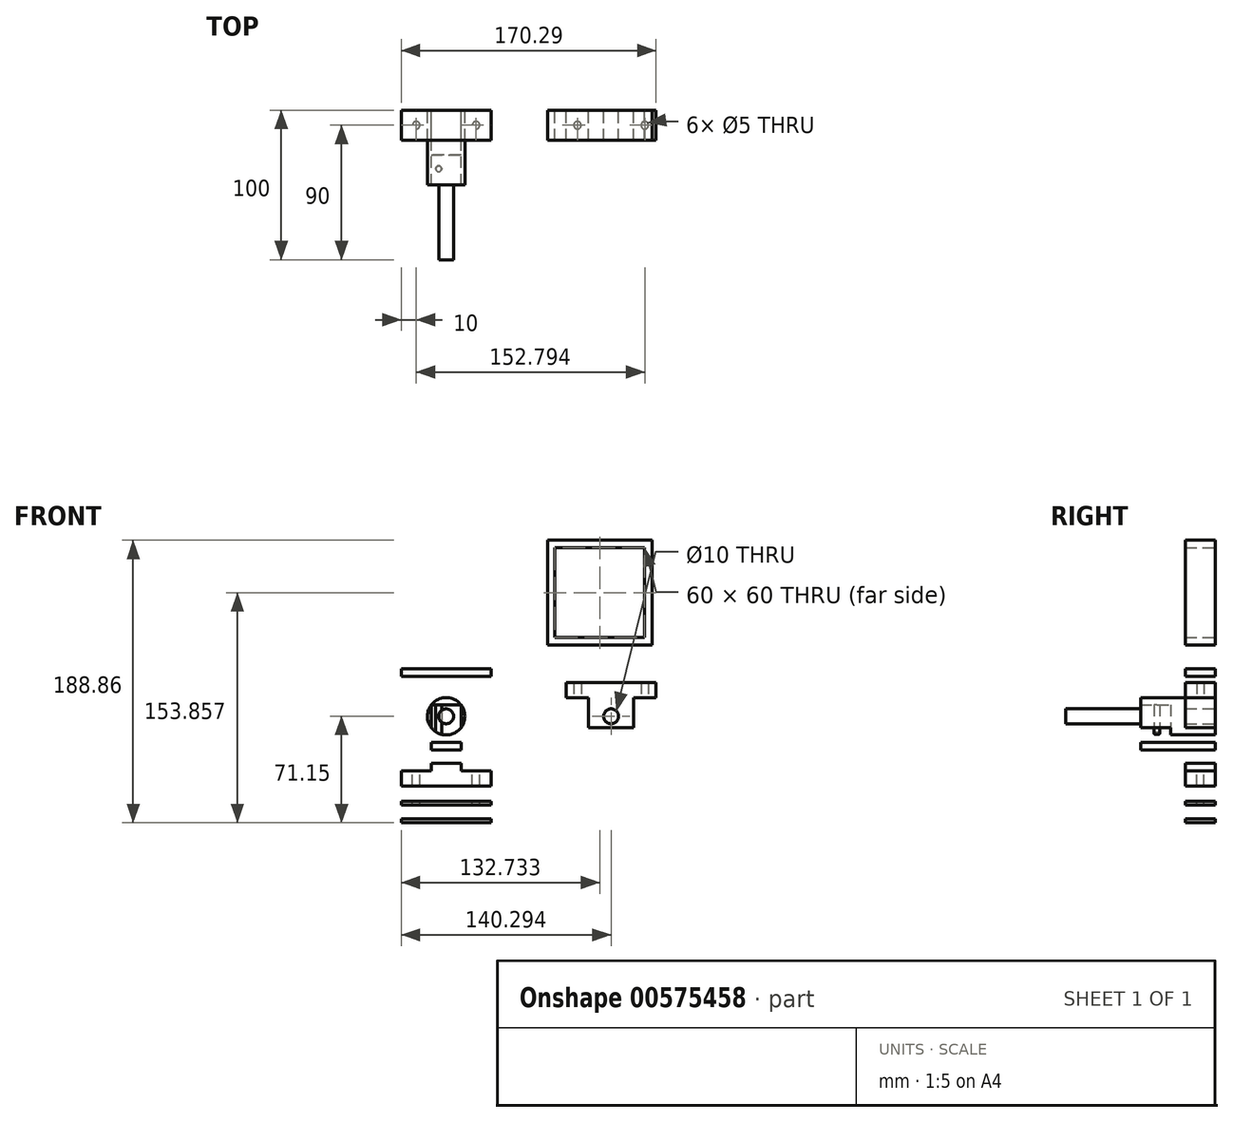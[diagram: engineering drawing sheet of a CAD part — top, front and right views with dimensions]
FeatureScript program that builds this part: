
annotation { "Feature Type Name" : "Feature", "Feature Type Description" : "" }
export const myFeature = defineFeature(function(context is Context, id is Id, definition is map)
    precondition{}
    {
        {
            var Q0;
            Q0=qCreatedBy(makeId("Front.planeOp"),FACE);
            var sketch = newSketch(context, id + "F0", { "sketchPlane" : qUnion([Q0])});
            skCircle(sketch, "E0", {"center": v(0, 0) * mm, "radius": 12.5 * mm});
            skCircle(sketch, "E1", {"center": v(110.3, 0) * mm, "radius": 5 * mm});
            skLineSegment(sketch, "E2.bottom", {"start": v(-30, 31.74) * mm, "end": v(30, 31.74) * mm});
            skLineSegment(sketch, "E2.top", {"start": v(-30, 26.74) * mm, "end": v(30, 26.74) * mm});
            skLineSegment(sketch, "E2.left", {"start": v(-30, 31.74) * mm, "end": v(-30, 26.74) * mm});
            skLineSegment(sketch, "E2.right", {"start": v(30, 31.74) * mm, "end": v(30, 26.74) * mm});
            skPoint(sketch, "E2.middle", {"position": v(0, 29.24) * mm});
            skLineSegment(sketch, "E3", {"start": v(110.3, 10) * mm, "end": v(110.3, -10) * mm, "construction": true});
            skCircle(sketch, "E4", {"center": v(110.3, 0) * mm, "radius": 12.5 * mm, "construction": true});
            skLineSegment(sketch, "E5", {"start": v(97.8, 0) * mm, "end": v(122.8, 0) * mm, "construction": true});
            skLineSegment(sketch, "E6", {"start": v(110.3, 12.5) * mm, "end": v(79.29, 12.5) * mm, "construction": true});
            skLineSegment(sketch, "E7", {"start": v(110.3, 5) * mm, "end": v(79.29, 5) * mm, "construction": true});
            skLineSegment(sketch, "E8", {"start": v(110.3, -5) * mm, "end": v(79.29, -5) * mm, "construction": true});
            skLineSegment(sketch, "E9", {"start": v(110.3, -12.5) * mm, "end": v(79.29, -12.5) * mm, "construction": true});
            skLineSegment(sketch, "E10", {"start": v(110.3, -7.5) * mm, "end": v(125.3, -7.5) * mm});
            skLineSegment(sketch, "E11", {"start": v(110.3, 22.5) * mm, "end": v(140.3, 22.5) * mm});
            skLineSegment(sketch, "E12", {"start": v(125.3, 12.5) * mm, "end": v(140.3, 12.5) * mm});
            skLineSegment(sketch, "E13", {"start": v(125.3, -7.5) * mm, "end": v(125.3, 12.5) * mm});
            skLineSegment(sketch, "E14", {"start": v(140.3, 22.5) * mm, "end": v(140.3, 12.5) * mm});
            skPoint(sketch, "E15.orphan", {"position": v(110.3, 12.5) * mm});
            skLineSegment(sketch, "E16.MirrorCS", {"start": v(95.3, 12.5) * mm, "end": v(80.3, 12.5) * mm});
            skLineSegment(sketch, "E17.MirrorCS", {"start": v(80.3, 22.5) * mm, "end": v(80.3, 12.5) * mm});
            skLineSegment(sketch, "E18.MirrorCS", {"start": v(110.3, 22.5) * mm, "end": v(80.3, 22.5) * mm});
            skLineSegment(sketch, "E19.MirrorCS", {"start": v(95.3, -7.5) * mm, "end": v(95.3, 12.5) * mm});
            skLineSegment(sketch, "E20.MirrorCS", {"start": v(110.3, -7.5) * mm, "end": v(95.3, -7.5) * mm});
            skLineSegment(sketch, "E21.top", {"start": v(0, -31.53) * mm, "end": v(10, -31.53) * mm});
            skLineSegment(sketch, "E21.right", {"start": v(10, -36.53) * mm, "end": v(10, -31.53) * mm});
            skLineSegment(sketch, "E22", {"start": v(10, -36.53) * mm, "end": v(30, -36.53) * mm});
            skLineSegment(sketch, "E23", {"start": v(30, -36.53) * mm, "end": v(30, -46.53) * mm});
            skLineSegment(sketch, "E24", {"start": v(30, -46.53) * mm, "end": v(0, -46.53) * mm});
            skLineSegment(sketch, "E25.MirrorCS", {"start": v(0, -31.53) * mm, "end": v(-10, -31.53) * mm});
            skLineSegment(sketch, "E26.MirrorCS", {"start": v(-10, -36.53) * mm, "end": v(-10, -31.53) * mm});
            skLineSegment(sketch, "E27.MirrorCS", {"start": v(-10, -36.53) * mm, "end": v(-30, -36.53) * mm});
            skLineSegment(sketch, "E28.MirrorCS", {"start": v(-30, -36.53) * mm, "end": v(-30, -46.53) * mm});
            skLineSegment(sketch, "E29.MirrorCS", {"start": v(-30, -46.53) * mm, "end": v(0, -46.53) * mm});
            skLineSegment(sketch, "E30", {"start": v(0, -22.52) * mm, "end": v(10, -22.52) * mm});
            skLineSegment(sketch, "E31", {"start": v(10, -22.52) * mm, "end": v(10, -17.52) * mm});
            skLineSegment(sketch, "E32", {"start": v(10, -17.52) * mm, "end": v(0, -17.52) * mm});
            skLineSegment(sketch, "E33.MirrorCS", {"start": v(-10, -17.52) * mm, "end": v(0, -17.52) * mm});
            skLineSegment(sketch, "E34.MirrorCS", {"start": v(0, -22.52) * mm, "end": v(-10, -22.52) * mm});
            skLineSegment(sketch, "E35.MirrorCS", {"start": v(-10, -22.52) * mm, "end": v(-10, -17.52) * mm});
            skLineSegment(sketch, "E36.bottom", {"start": v(132.73, 52.7) * mm, "end": v(72.73, 52.7) * mm});
            skLineSegment(sketch, "E36.top", {"start": v(132.73, 112.7) * mm, "end": v(72.73, 112.7) * mm});
            skLineSegment(sketch, "E36.left", {"start": v(132.73, 52.7) * mm, "end": v(132.73, 112.7) * mm});
            skLineSegment(sketch, "E36.right", {"start": v(72.73, 52.7) * mm, "end": v(72.73, 112.7) * mm});
            skPoint(sketch, "E36.middle", {"position": v(102.73, 82.7) * mm});
            skLineSegment(sketch, "E37.bottom", {"start": v(67.73, 117.7) * mm, "end": v(137.73, 117.7) * mm});
            skLineSegment(sketch, "E37.top", {"start": v(67.73, 47.7) * mm, "end": v(137.73, 47.7) * mm});
            skLineSegment(sketch, "E37.left", {"start": v(67.73, 117.7) * mm, "end": v(67.73, 47.7) * mm});
            skLineSegment(sketch, "E37.right", {"start": v(137.73, 117.7) * mm, "end": v(137.73, 47.7) * mm});
            skLineSegment(sketch, "E38.bottom", {"start": v(-30, -59.43) * mm, "end": v(30, -59.43) * mm});
            skLineSegment(sketch, "E38.top", {"start": v(-30, -56.93) * mm, "end": v(30, -56.93) * mm});
            skLineSegment(sketch, "E38.left", {"start": v(-30, -59.43) * mm, "end": v(-30, -56.93) * mm});
            skLineSegment(sketch, "E38.right", {"start": v(30, -59.43) * mm, "end": v(30, -56.93) * mm});
            skLineSegment(sketch, "E39.MirrorCS", {"start": v(-30, -68.65) * mm, "end": v(30, -68.65) * mm});
            skLineSegment(sketch, "E40.MirrorCS", {"start": v(-30, -68.65) * mm, "end": v(-30, -71.15) * mm});
            skLineSegment(sketch, "E41.MirrorCS", {"start": v(-30, -71.15) * mm, "end": v(30, -71.15) * mm});
            skLineSegment(sketch, "E42.MirrorCS", {"start": v(30, -68.65) * mm, "end": v(30, -71.15) * mm});
            skSolve(sketch);
        }
        {
            var Q0;
            Q0=makeQuery(id+"F0.imprint","IMPRINT",FACE,{"disambiguationData":[TD([[makeQuery(id+"F0.imprint","IMPRINT",EDGE,{"derivedFrom":sQuery(id+"F0.wireOp",EDGE,"E1")}),-1.0]])]});
            var Q1;
            Q1=makeQuery(id+"F0.imprint","IMPRINT",FACE,{"disambiguationData":[TD([[makeQuery(id+"F0.imprint","IMPRINT",EDGE,{"derivedFrom":sQuery(id+"F0.wireOp",EDGE,"E2.bottom")}),-1.0]])]});
            var Q2;
            Q2=makeQuery(id+"F0.imprint","IMPRINT",FACE,{"disambiguationData":[TD([[makeQuery(id+"F0.imprint","IMPRINT",EDGE,{"derivedFrom":sQuery(id+"F0.wireOp",EDGE,"E21.top")}),-1.0]])]});
            var Q3;
            Q3=makeQuery(id+"F0.imprint","IMPRINT",FACE,{"disambiguationData":[TD([[makeQuery(id+"F0.imprint","IMPRINT",EDGE,{"derivedFrom":sQuery(id+"F0.wireOp",EDGE,"E36.bottom")}),1.0]])]});
            var Q4;
            Q4=makeQuery(id+"F0.imprint","IMPRINT",FACE,{"disambiguationData":[TD([[makeQuery(id+"F0.imprint","IMPRINT",EDGE,{"derivedFrom":sQuery(id+"F0.wireOp",EDGE,"E38.bottom")}),1.0]])]});
            var Q5;
            Q5=makeQuery(id+"F0.imprint","IMPRINT",FACE,{"disambiguationData":[TD([[makeQuery(id+"F0.imprint","IMPRINT",EDGE,{"derivedFrom":sQuery(id+"F0.wireOp",EDGE,"E39.MirrorCS")}),-1.0]])]});
            extrude(context, id + "F1", {"entities" : qUnion([Q0, Q1, Q2, Q3, Q4, Q5]), "depth" : 20 * mm, "offsetDistance" : 25 * mm});
        }
        {
            var Q0;
            Q0=makeQuery(id+"F0.imprint","IMPRINT",FACE,{"disambiguationData":[TD([[makeQuery(id+"F0.imprint","IMPRINT",EDGE,{"derivedFrom":sQuery(id+"F0.wireOp",EDGE,"E0")}),1.0]])]});
            extrude(context, id + "F2", {"entities" : qUnion([Q0]), "depth" : 50 * mm, "offsetDistance" : 25 * mm});
        }
        {
            var Q0;
            Q0=makeQuery(id+"F2.opExtrude","CAP_FACE",FACE,{"disambiguationData":[OSD([sQuery(id+"F0.wireOp",EDGE,"E0")])],"isStart":false});
            var sketch = newSketch(context, id + "F3", { "sketchPlane" : qUnion([Q0])});
            skCircle(sketch, "E43", {"center": v(0, 0) * mm, "radius": 5 * mm});
            skSolve(sketch);
        }
        {
            var Q0;
            Q0=makeQuery(id+"F3.imprint","IMPRINT",FACE,{"disambiguationData":[TD([[makeQuery(id+"F3.imprint","IMPRINT",EDGE,{"derivedFrom":sQuery(id+"F3.wireOp",EDGE,"E43")}),1.0]])]});
            extrude(context, id + "F4", {"entities" : qUnion([Q0]), "operationType" : NewBodyOperationType.ADD, "depth" : 50 * mm, "offsetDistance" : 25 * mm});
        }
        {
            var Q0;
            Q0=makeQuery(id+"F0.imprint","IMPRINT",FACE,{"disambiguationData":[TD([[makeQuery(id+"F0.imprint","IMPRINT",EDGE,{"derivedFrom":sQuery(id+"F0.wireOp",EDGE,"E30")}),1.0]])]});
            extrude(context, id + "F5", {"entities" : qUnion([Q0]), "depth" : 50 * mm, "offsetDistance" : 25 * mm});
        }
        {
            var Q0;
            Q0=makeQuery(id+"F1.opExtrude","SWEPT_FACE",FACE,{"disambiguationData":[OSD([sQuery(id+"F0.wireOp",EDGE,"E27.MirrorCS")])]});
            var sketch = newSketch(context, id + "F6", { "sketchPlane" : qUnion([Q0])});
            skCircle(sketch, "E44", {"center": v(-20, -10) * mm, "radius": 2.5 * mm});
            skSolve(sketch);
        }
        {
            var Q0;
            Q0=makeQuery(id+"F1.opExtrude","SWEPT_FACE",FACE,{"disambiguationData":[OSD([sQuery(id+"F0.wireOp",EDGE,"E22")])]});
            var sketch = newSketch(context, id + "F7", { "sketchPlane" : qUnion([Q0])});
            skCircle(sketch, "E45", {"center": v(20, -10) * mm, "radius": 2.5 * mm});
            skSolve(sketch);
        }
        {
            var Q0;
            Q0=makeQuery(id+"F6.imprint","IMPRINT",FACE,{"disambiguationData":[TD([[makeQuery(id+"F6.imprint","IMPRINT",EDGE,{"derivedFrom":sQuery(id+"F6.wireOp",EDGE,"E44")}),1.0]])]});
            var Q1;
            Q1=makeQuery(id+"F7.imprint","IMPRINT",FACE,{"disambiguationData":[TD([[makeQuery(id+"F7.imprint","IMPRINT",EDGE,{"derivedFrom":sQuery(id+"F7.wireOp",EDGE,"E45")}),1.0]])]});
            extrude(context, id + "F8", {"entities" : qUnion([Q0, Q1]), "operationType" : NewBodyOperationType.REMOVE, "oppositeDirection" : true, "depth" : 25 * mm, "offsetDistance" : 25 * mm});
        }
        {
            var Q0;
            Q0=makeQuery(id+"F1.opExtrude","SWEPT_FACE",FACE,{"disambiguationData":[OSD([sQuery(id+"F0.wireOp",EDGE,"E12")])]});
            var sketch = newSketch(context, id + "F9", { "sketchPlane" : qUnion([Q0])});
            skCircle(sketch, "E46", {"center": v(132.8, 10) * mm, "radius": 2.5 * mm});
            skPoint(sketch, "E46.centerSnap0", {"position": v(132.8, 20) * mm});
            skPoint(sketch, "E46.centerSnap1", {"position": v(125.3, 10) * mm});
            skSolve(sketch);
        }
        {
            var Q0;
            Q0=makeQuery(id+"F1.opExtrude","SWEPT_FACE",FACE,{"disambiguationData":[OSD([sQuery(id+"F0.wireOp",EDGE,"E16.MirrorCS")])]});
            var sketch = newSketch(context, id + "F10", { "sketchPlane" : qUnion([Q0])});
            skCircle(sketch, "E47", {"center": v(87.8, 10) * mm, "radius": 2.5 * mm});
            skPoint(sketch, "E47.centerSnap0", {"position": v(80.3, 10) * mm});
            skPoint(sketch, "E47.centerSnap1", {"position": v(87.8, 20) * mm});
            skSolve(sketch);
        }
        {
            var Q0;
            Q0=makeQuery(id+"F10.imprint","IMPRINT",FACE,{"disambiguationData":[TD([[makeQuery(id+"F10.imprint","IMPRINT",EDGE,{"derivedFrom":sQuery(id+"F10.wireOp",EDGE,"E47")}),1.0]])]});
            var Q1;
            Q1=makeQuery(id+"F9.imprint","IMPRINT",FACE,{"disambiguationData":[TD([[makeQuery(id+"F9.imprint","IMPRINT",EDGE,{"derivedFrom":sQuery(id+"F9.wireOp",EDGE,"E46")}),1.0]])]});
            extrude(context, id + "F11", {"entities" : qUnion([Q0, Q1]), "operationType" : NewBodyOperationType.REMOVE, "oppositeDirection" : true, "depth" : 25 * mm, "offsetDistance" : 25 * mm});
        }
        {
            var Q0;
            Q0=makeQuery(id+"F5.opExtrude","SWEPT_FACE",FACE,{"disambiguationData":[OSD([sQuery(id+"F0.wireOp",EDGE,"E32"),sQuery(id+"F0.wireOp",EDGE,"E33.MirrorCS")])]});
            var sketch = newSketch(context, id + "F12", { "sketchPlane" : qUnion([Q0])});
            skLineSegment(sketch, "E48", {"start": v(-10, -30) * mm, "end": v(10, -30) * mm});
            skCircle(sketch, "E49", {"center": v(5, -39.13) * mm, "radius": 1.93 * mm});
            skPoint(sketch, "E50.orphan", {"position": v(0, -50) * mm});
            skCircle(sketch, "E51.MirrorC", {"center": v(-5, -39.13) * mm, "radius": 1.93 * mm});
            skSolve(sketch);
        }
        {
            var Q0;
            Q0=makeQuery(id+"F12.imprint","IMPRINT",FACE,{"disambiguationData":[TD([[makeQuery(id+"F12.imprint","IMPRINT",EDGE,{"derivedFrom":sQuery(id+"F12.wireOp",EDGE,"E51.MirrorC")}),-1.0]])]});
            var Q1;
            Q1=makeQuery(id+"F12.imprint","IMPRINT",FACE,{"disambiguationData":[TD([[makeQuery(id+"F12.imprint","IMPRINT",EDGE,{"derivedFrom":sQuery(id+"F12.wireOp",EDGE,"E49")}),1.0]])]});
            extrude(context, id + "F13", {"entities" : qUnion([Q0, Q1]), "operationType" : NewBodyOperationType.REMOVE, "depth" : 25 * mm, "offsetDistance" : 25 * mm});
        }
    });
